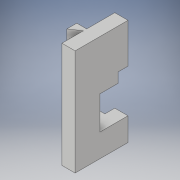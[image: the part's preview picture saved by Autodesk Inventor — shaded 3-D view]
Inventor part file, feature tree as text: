
AUTODESK INVENTOR PART (.ipt)
format: ipt  version: 2019 (Build 230136000, 136)  size: 132,608 bytes
history: native  units: mm
features: extrude x3, sketch x3, projected_geometry x2
ambient origin geometry x8: Origin, YZ Plane, XZ Plane, XY Plane, X Axis, Y Axis, Z Axis, Center Point
bodies: Solid1 (feature_tree)
feature tree (8):
  extrude  "Extrusion1"  Depth=4.0mm
  extrude  "Extrusion2"  Depth=3.0mm
  extrude  "Extrusion3"  Depth=8.5mm
  sketch  "Sketch1"  dims[d0=16.0mm d1=4.0mm]
  sketch  "Sketch2"  dims[d2=6.5mm d3=3.0mm]
  projected_geometry  "Projected Loop1"
  sketch  "Sketch3"  dims[d4=3.0mm d5=8.5mm d6=32.0mm d7=0.0mm d8=25.0mm d9=5.5mm d10=3.0mm d11=0.0mm d12=12.0mm d13=15.0mm d14=3.0mm d15=4.0mm d16=0.0mm]
  projected_geometry  "Projected Loop2"
